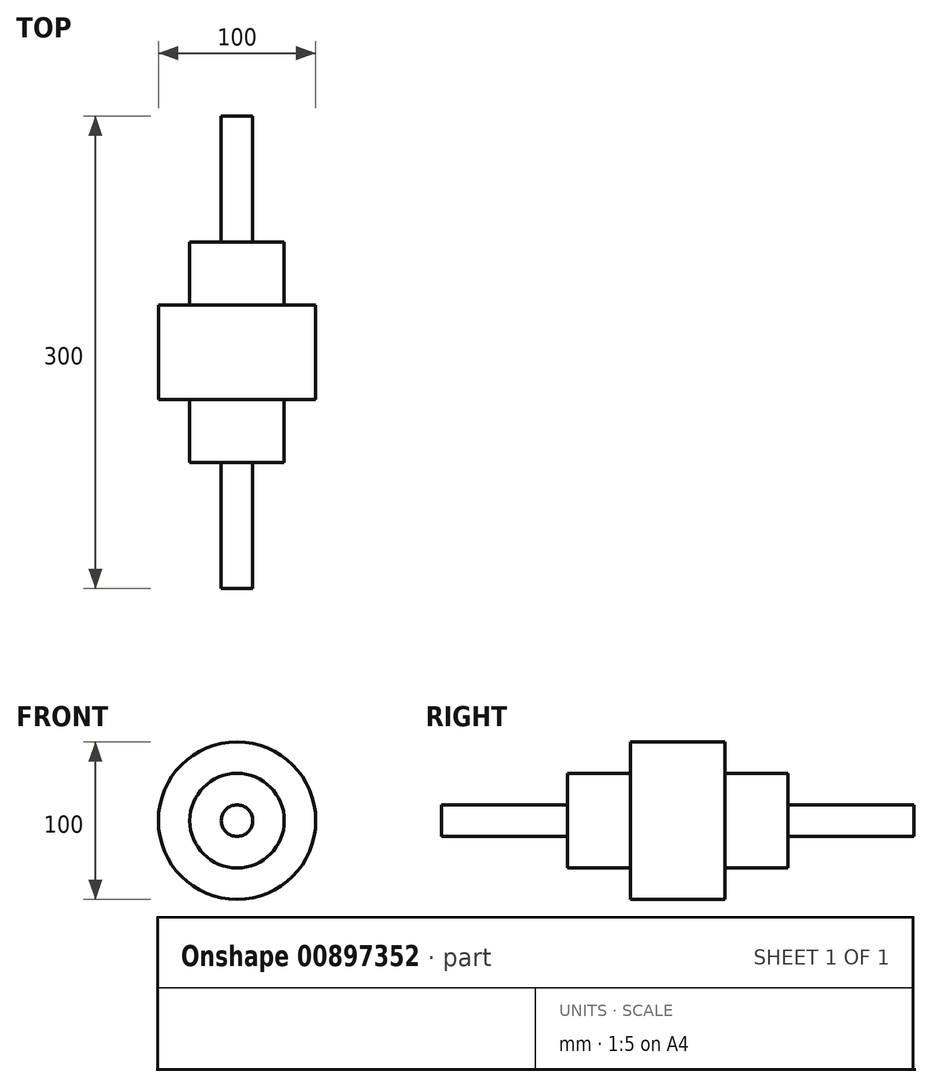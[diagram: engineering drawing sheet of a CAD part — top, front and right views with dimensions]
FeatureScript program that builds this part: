
annotation { "Feature Type Name" : "Feature", "Feature Type Description" : "" }
export const myFeature = defineFeature(function(context is Context, id is Id, definition is map)
    precondition{}
    {
        {
            var Q0;
            Q0=qCreatedBy(makeId("Front.planeOp"),FACE);
            var sketch = newSketch(context, id + "F0", { "sketchPlane" : qUnion([Q0])});
            skCircle(sketch, "E0", {"center": v(0, 0) * mm, "radius": 50 * mm});
            skSolve(sketch);
        }
        {
            var Q0;
            Q0 = qSketchRegion(id + "F0", true);
            extrude(context, id + "F1", {"entities" : qUnion([Q0]), "depth" : 30 * mm, "offsetDistance" : 25.4 * mm});
        }
        {
            var Q0;
            Q0=makeQuery(id+"F1.opExtrude","CAP_FACE",FACE,{"disambiguationData":[OSD([sQuery(id+"F0.wireOp",EDGE,"E0")])],"isStart":true});
            extrude(context, id + "F2", {"entities" : qUnion([Q0]), "operationType" : NewBodyOperationType.ADD, "depth" : 30 * mm, "offsetDistance" : 25.4 * mm});
        }
        {
            var Q0;
            Q0=makeQuery(id+"F1.opExtrude","CAP_FACE",FACE,{"disambiguationData":[OSD([sQuery(id+"F0.wireOp",EDGE,"E0")])],"isStart":false});
            var sketch = newSketch(context, id + "F3", { "sketchPlane" : qUnion([Q0])});
            skCircle(sketch, "E1", {"center": v(0, 0) * mm, "radius": 30 * mm});
            skSolve(sketch);
        }
        {
            var Q0;
            Q0=makeQuery(id+"F3.imprint","IMPRINT",FACE,{"disambiguationData":[TD([[makeQuery(id+"F3.imprint","IMPRINT",EDGE,{"derivedFrom":sQuery(id+"F3.wireOp",EDGE,"E1")}),1.0]])]});
            extrude(context, id + "F4", {"entities" : qUnion([Q0]), "operationType" : NewBodyOperationType.ADD, "depth" : 40 * mm, "offsetDistance" : 25.4 * mm});
        }
        {
            var Q0;
            Q0=makeQuery(id+"F4.opExtrude","CAP_FACE",FACE,{"disambiguationData":[OSD([sQuery(id+"F3.wireOp",EDGE,"E1")])],"isStart":false});
            var sketch = newSketch(context, id + "F5", { "sketchPlane" : qUnion([Q0])});
            skCircle(sketch, "E2", {"center": v(0, 0) * mm, "radius": 10 * mm});
            skSolve(sketch);
        }
        {
            var Q0;
            Q0=makeQuery(id+"F5.imprint","IMPRINT",FACE,{"disambiguationData":[TD([[makeQuery(id+"F5.imprint","IMPRINT",EDGE,{"derivedFrom":sQuery(id+"F5.wireOp",EDGE,"E2")}),1.0]])]});
            extrude(context, id + "F6", {"entities" : qUnion([Q0]), "operationType" : NewBodyOperationType.ADD, "depth" : 80 * mm, "offsetDistance" : 25.4 * mm});
        }
        {
            var Q0;
            Q0=makeQuery(id+"F2.opExtrude","CAP_FACE",FACE,{"disambiguationData":[OSD([sQuery(id+"F0.wireOp",EDGE,"E0")])],"isStart":false});
            var sketch = newSketch(context, id + "F7", { "sketchPlane" : qUnion([Q0])});
            skCircle(sketch, "E3", {"center": v(0, 0) * mm, "radius": 30 * mm});
            skSolve(sketch);
        }
        {
            var Q0;
            Q0=makeQuery(id+"F7.imprint","IMPRINT",FACE,{"disambiguationData":[TD([[makeQuery(id+"F7.imprint","IMPRINT",EDGE,{"derivedFrom":sQuery(id+"F7.wireOp",EDGE,"E3")}),1.0]])]});
            extrude(context, id + "F8", {"entities" : qUnion([Q0]), "operationType" : NewBodyOperationType.ADD, "depth" : 40 * mm, "offsetDistance" : 25.4 * mm});
        }
        {
            var Q0;
            Q0=makeQuery(id+"F8.opExtrude","CAP_FACE",FACE,{"disambiguationData":[OSD([sQuery(id+"F7.wireOp",EDGE,"E3")])],"isStart":false});
            var sketch = newSketch(context, id + "F9", { "sketchPlane" : qUnion([Q0])});
            skCircle(sketch, "E4", {"center": v(0, 0) * mm, "radius": 10 * mm});
            skSolve(sketch);
        }
        {
            var Q0;
            Q0=makeQuery(id+"F9.imprint","IMPRINT",FACE,{"disambiguationData":[TD([[makeQuery(id+"F9.imprint","IMPRINT",EDGE,{"derivedFrom":sQuery(id+"F9.wireOp",EDGE,"E4")}),1.0]])]});
            extrude(context, id + "F10", {"entities" : qUnion([Q0]), "operationType" : NewBodyOperationType.ADD, "depth" : 80 * mm, "offsetDistance" : 25.4 * mm});
        }
    });
